# Revit family: 13. Секция фильтра ANR F1-9
name_source: partatom
category: Оборудование
revit_build: Autodesk Revit 2016 (Build: 20161004_0715(x64)
units: mm (PartAtom-declared; Revit-internal decimal feet)

## family parameters
Всегда вертикально = Да
На основе рабочей плоскости = Нет
Общий = Нет
При загрузке вырезать с полостями = Нет
Размер круглого соединителя = Использовать диаметр
Тип детали = Нормальный
Точка расчета площади = Нет

## types (50) — shared parameters
h = 130 мм
Единица измерения = шт.
Завод изготовитель = KORF
Ключевая пометка = Вентиляция
Материал = Сталь серая
Наименование и тех.хар-ка = Секция фильтра
Раздел = ОВ
Синий = Синий
высота ножек = 120 мм
№8 = Нет

## per-type parameters (varying)
| type | А | А1 | Б | Б1 | Высота | Д | Д1 | Середина | Фильтрующая вставка | Ширина | №12 | №20 | №25 | №30 | №35 | №40 | №45 | №6 | №7 |
| ANR 6 F1 | 1100 мм | 1080 мм | 1100 мм | 1080 мм | 1025 мм | 575 мм | 555 мм | 670 мм | EU4 | 1025 мм | Нет | Нет | Нет | Нет | Нет | Нет | Нет | Да | Нет |
| ANR 7 F1 | 1100 мм | 1080 мм | 1320 мм | 1300 мм | 1245 мм | 1100 мм | 1080 мм | 780 мм | EU4 | 1025 мм | Нет | Нет | Нет | Нет | Нет | Нет | Нет | Нет | Да |
| ANR 8 F1 | 1320 мм | 1300 мм | 1320 мм | 1300 мм | 1245 мм | 1100 мм | 1080 мм | 780 мм | EU4 | 1245 мм | Нет | Нет | Нет | Нет | Нет | Нет | Нет | Нет | Да |
| ANR 20 F1 | 1660 мм | 1640 мм | 1660 мм | 1640 мм | 1585 мм | 575 мм | 555 мм | 950 мм | EU4 | 1585 мм | Нет | Да | Нет | Нет | Нет | Нет | Нет | Нет | Нет |
| ANR 25 F1 | 2045 мм | 2025 мм | 2045 мм | 2025 мм | 1970 мм | 575 мм | 555 мм | 1143 мм | EU4 | 1970 мм | Нет | Нет | Да | Нет | Нет | Нет | Нет | Нет | Нет |
| ANR 30 F1 | 2485 мм | 2465 мм | 2045 мм | 2025 мм | 1970 мм | 575 мм | 555 мм | 1143 мм | EU4 | 2410 мм | Нет | Нет | Нет | Да | Нет | Нет | Нет | Нет | Нет |
| ANR 35 F1 | 2485 мм | 2465 мм | 2485 мм | 2465 мм | 2410 мм | 575 мм | 555 мм | 1363 мм | EU4 | 2410 мм | Нет | Нет | Нет | Нет | Да | Нет | Нет | Нет | Нет |
| ANR 12 F1 | 1435 мм | 1415 мм | 1435 мм | 1415 мм | 1360 мм | 575 мм | 555 мм | 838 мм | EU4 | 1360 мм | Да | Нет | Нет | Нет | Нет | Нет | Нет | Нет | Нет |
| ANR 40 F1 | 3320 мм | 3300 мм | 3320 мм | 3300 мм | 3245 мм | 575 мм | 555 мм | 1780 мм | EU4 | 3245 мм | Нет | Нет | Нет | Нет | Нет | Да | Нет | Нет | Нет |
| ANR 45 F1 | 3320 мм | 3300 мм | 4090 мм | 4070 мм | 4015 мм | 575 мм | 555 мм | 2165 мм | EU4 | 3245 мм | Нет | Нет | Нет | Нет | Нет | Нет | Да | Нет | Нет |
| ANR 6 F5 | 1100 мм | 1080 мм | 1100 мм | 1080 мм | 1025 мм | 1100 мм | 1080 мм | 670 мм | EU5 | 1025 мм | Нет | Нет | Нет | Нет | Нет | Нет | Нет | Да | Нет |
| ANR 6 F7 | 1100 мм | 1080 мм | 1100 мм | 1080 мм | 1025 мм | 1100 мм | 1080 мм | 670 мм | EU7 | 1025 мм | Нет | Нет | Нет | Нет | Нет | Нет | Нет | Да | Нет |
| ANR 6 F8 | 1100 мм | 1080 мм | 1100 мм | 1080 мм | 1025 мм | 1100 мм | 1080 мм | 670 мм | EU8 | 1025 мм | Нет | Нет | Нет | Нет | Нет | Нет | Нет | Да | Нет |
| ANR 6 F9 | 1100 мм | 1080 мм | 1100 мм | 1080 мм | 1025 мм | 1100 мм | 1080 мм | 670 мм | EU9 | 1025 мм | Нет | Нет | Нет | Нет | Нет | Нет | Нет | Да | Нет |
| ANR 7 F5 | 1100 мм | 1080 мм | 1320 мм | 1300 мм | 1245 мм | 1100 мм | 1080 мм | 780 мм | EU5 | 1025 мм | Нет | Нет | Нет | Нет | Нет | Нет | Нет | Нет | Да |
| ANR 7 F7 | 1100 мм | 1080 мм | 1320 мм | 1300 мм | 1245 мм | 1100 мм | 1080 мм | 780 мм | EU7 | 1025 мм | Нет | Нет | Нет | Нет | Нет | Нет | Нет | Нет | Да |
| ANR 7 F8 | 1100 мм | 1080 мм | 1320 мм | 1300 мм | 1245 мм | 1100 мм | 1080 мм | 780 мм | EU8 | 1025 мм | Нет | Нет | Нет | Нет | Нет | Нет | Нет | Нет | Да |
| ANR 7 F9 | 1100 мм | 1080 мм | 1320 мм | 1300 мм | 1245 мм | 1100 мм | 1080 мм | 780 мм | EU9 | 1025 мм | Нет | Нет | Нет | Нет | Нет | Нет | Нет | Нет | Да |
| ANR 8 F5 | 1320 мм | 1300 мм | 1320 мм | 1300 мм | 1245 мм | 1100 мм | 1080 мм | 780 мм | EU5 | 1245 мм | Нет | Нет | Нет | Нет | Нет | Нет | Нет | Нет | Да |
| ANR 8 F7 | 1320 мм | 1300 мм | 1320 мм | 1300 мм | 1245 мм | 1100 мм | 1080 мм | 780 мм | EU7 | 1245 мм | Нет | Нет | Нет | Нет | Нет | Нет | Нет | Нет | Да |
| ANR 8 F8 | 1320 мм | 1300 мм | 1320 мм | 1300 мм | 1245 мм | 1100 мм | 1080 мм | 780 мм | EU8 | 1245 мм | Нет | Нет | Нет | Нет | Нет | Нет | Нет | Нет | Да |
| ANR 8 F9 | 1320 мм | 1300 мм | 1320 мм | 1300 мм | 1245 мм | 1100 мм | 1080 мм | 780 мм | EU9 | 1245 мм | Нет | Нет | Нет | Нет | Нет | Нет | Нет | Нет | Да |
| ANR 12 F5 | 1435 мм | 1415 мм | 1435 мм | 1415 мм | 1360 мм | 1100 мм | 1080 мм | 838 мм | EU5 | 1360 мм | Да | Нет | Нет | Нет | Нет | Нет | Нет | Нет | Нет |
| ANR 12 F7 | 1435 мм | 1415 мм | 1435 мм | 1415 мм | 1360 мм | 1100 мм | 1080 мм | 838 мм | EU7 | 1360 мм | Да | Нет | Нет | Нет | Нет | Нет | Нет | Нет | Нет |
| ANR 12 F8 | 1435 мм | 1415 мм | 1435 мм | 1415 мм | 1360 мм | 1100 мм | 1080 мм | 838 мм | EU8 | 1360 мм | Да | Нет | Нет | Нет | Нет | Нет | Нет | Нет | Нет |
| ANR 12 F9 | 1435 мм | 1415 мм | 1435 мм | 1415 мм | 1360 мм | 1100 мм | 1080 мм | 838 мм | EU9 | 1360 мм | Да | Нет | Нет | Нет | Нет | Нет | Нет | Нет | Нет |
| ANR 20 F5 | 1660 мм | 1640 мм | 1660 мм | 1640 мм | 1585 мм | 1100 мм | 1080 мм | 950 мм | EU5 | 1585 мм | Нет | Да | Нет | Нет | Нет | Нет | Нет | Нет | Нет |
| ANR 20 F7 | 1660 мм | 1640 мм | 1660 мм | 1640 мм | 1585 мм | 1100 мм | 1080 мм | 950 мм | EU7 | 1585 мм | Нет | Да | Нет | Нет | Нет | Нет | Нет | Нет | Нет |
| ANR 20 F8 | 1660 мм | 1640 мм | 1660 мм | 1640 мм | 1585 мм | 1100 мм | 1080 мм | 950 мм | EU8 | 1585 мм | Нет | Да | Нет | Нет | Нет | Нет | Нет | Нет | Нет |
| ANR 20 F9 | 1660 мм | 1640 мм | 1660 мм | 1640 мм | 1585 мм | 1100 мм | 1080 мм | 950 мм | EU9 | 1585 мм | Нет | Да | Нет | Нет | Нет | Нет | Нет | Нет | Нет |
| ANR 25 F5 | 2045 мм | 2025 мм | 2045 мм | 2025 мм | 1970 мм | 1100 мм | 1080 мм | 1143 мм | EU5 | 1970 мм | Нет | Нет | Да | Нет | Нет | Нет | Нет | Нет | Нет |
| ANR 25 F7 | 2045 мм | 2025 мм | 2045 мм | 2025 мм | 1970 мм | 1100 мм | 1080 мм | 1143 мм | EU7 | 1970 мм | Нет | Нет | Да | Нет | Нет | Нет | Нет | Нет | Нет |
| ANR 25 F8 | 2045 мм | 2025 мм | 2045 мм | 2025 мм | 1970 мм | 1100 мм | 1080 мм | 1143 мм | EU8 | 1970 мм | Нет | Нет | Да | Нет | Нет | Нет | Нет | Нет | Нет |
| ANR 25 F9 | 2045 мм | 2025 мм | 2045 мм | 2025 мм | 1970 мм | 1100 мм | 1080 мм | 1143 мм | EU9 | 1970 мм | Нет | Нет | Да | Нет | Нет | Нет | Нет | Нет | Нет |
| ANR 30 F5 | 2485 мм | 2465 мм | 2045 мм | 2025 мм | 1970 мм | 1100 мм | 1080 мм | 1143 мм | EU5 | 2410 мм | Нет | Нет | Нет | Да | Нет | Нет | Нет | Нет | Нет |
| ANR 30 F7 | 2485 мм | 2465 мм | 2045 мм | 2025 мм | 1970 мм | 1100 мм | 1080 мм | 1143 мм | EU7 | 2410 мм | Нет | Нет | Нет | Да | Нет | Нет | Нет | Нет | Нет |
| ANR 30 F8 | 2485 мм | 2465 мм | 2045 мм | 2025 мм | 1970 мм | 1100 мм | 1080 мм | 1143 мм | EU8 | 2410 мм | Нет | Нет | Нет | Да | Нет | Нет | Нет | Нет | Нет |
| ANR 30 F9 | 2485 мм | 2465 мм | 2045 мм | 2025 мм | 1970 мм | 1100 мм | 1080 мм | 1143 мм | EU9 | 2410 мм | Нет | Нет | Нет | Да | Нет | Нет | Нет | Нет | Нет |
| ANR 35 F5 | 2485 мм | 2465 мм | 2485 мм | 2465 мм | 2410 мм | 1100 мм | 1080 мм | 1363 мм | EU5 | 2410 мм | Нет | Нет | Нет | Нет | Да | Нет | Нет | Нет | Нет |
| ANR 35 F7 | 2485 мм | 2465 мм | 2485 мм | 2465 мм | 2410 мм | 1100 мм | 1080 мм | 1363 мм | EU7 | 2410 мм | Нет | Нет | Нет | Нет | Да | Нет | Нет | Нет | Нет |
| ANR 35 F8 | 2485 мм | 2465 мм | 2485 мм | 2465 мм | 2410 мм | 1100 мм | 1080 мм | 1363 мм | EU8 | 2410 мм | Нет | Нет | Нет | Нет | Да | Нет | Нет | Нет | Нет |
| ANR 35 F9 | 2485 мм | 2465 мм | 2485 мм | 2465 мм | 2410 мм | 1100 мм | 1080 мм | 1363 мм | EU9 | 2410 мм | Нет | Нет | Нет | Нет | Да | Нет | Нет | Нет | Нет |
| ANR 40 F5 | 3320 мм | 3300 мм | 3320 мм | 3300 мм | 3245 мм | 1100 мм | 1080 мм | 1780 мм | EU5 | 3245 мм | Нет | Нет | Нет | Нет | Нет | Да | Нет | Нет | Нет |
| ANR 40 F7 | 3320 мм | 3300 мм | 3320 мм | 3300 мм | 3245 мм | 1100 мм | 1080 мм | 1780 мм | EU7 | 3245 мм | Нет | Нет | Нет | Нет | Нет | Да | Нет | Нет | Нет |
| ANR 40 F8 | 3320 мм | 3300 мм | 3320 мм | 3300 мм | 3245 мм | 1100 мм | 1080 мм | 1780 мм | EU8 | 3245 мм | Нет | Нет | Нет | Нет | Нет | Да | Нет | Нет | Нет |
| ANR 40 F9 | 3320 мм | 3300 мм | 3320 мм | 3300 мм | 3245 мм | 1100 мм | 1080 мм | 1780 мм | EU9 | 3245 мм | Нет | Нет | Нет | Нет | Нет | Да | Нет | Нет | Нет |
| ANR 45 F5 | 3320 мм | 3300 мм | 4090 мм | 4070 мм | 4015 мм | 1100 мм | 1080 мм | 2165 мм | EU5 | 3245 мм | Нет | Нет | Нет | Нет | Нет | Нет | Да | Нет | Нет |
| ANR 45 F7 | 3320 мм | 3300 мм | 4090 мм | 4070 мм | 4015 мм | 1100 мм | 1080 мм | 2165 мм | EU7 | 3245 мм | Нет | Нет | Нет | Нет | Нет | Нет | Да | Нет | Нет |
| ANR 45 F8 | 3320 мм | 3300 мм | 4090 мм | 4070 мм | 4015 мм | 1100 мм | 1080 мм | 2165 мм | EU8 | 3245 мм | Нет | Нет | Нет | Нет | Нет | Нет | Да | Нет | Нет |
| ANR 45 F9 | 3320 мм | 3300 мм | 4090 мм | 4070 мм | 4015 мм | 1100 мм | 1080 мм | 2165 мм | EU9 | 3245 мм | Нет | Нет | Нет | Нет | Нет | Нет | Да | Нет | Нет |

note: column(s) folded — value = type name in every type: Тип, марка, обозначение
